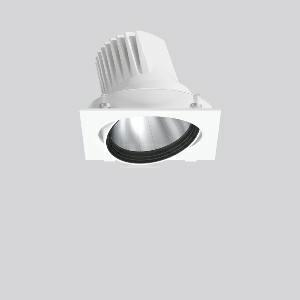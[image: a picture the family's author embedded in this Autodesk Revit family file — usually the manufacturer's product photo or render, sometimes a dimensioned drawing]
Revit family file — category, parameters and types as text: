
# Revit family: magcardo_maxi_722188_002_1_5fc1
name_source: partatom
category: Lighting Fixtures
units: mm (PartAtom-declared; Revit-internal decimal feet)

## family parameters
Cut with Voids When Loaded = No
Host = Face
Light Source = No
Part Type = Normal
Room Calculation Point = No
Round Connector Dimension = Use Diameter
Shared = No

## types (1)
- MAGCARDO maxi (1 x LED Modul 940, 3500 lm, 4000)
    Apparent Load = 25 VA
    Approval mark = CE
    CIE Flux Codes = 100 100 100 100 100
    Color Rendering = 92
    Color Temperature = 4000
    Default Elevation = 1800 mm
    Description = Series: MAGCARDO maxi
Projector unit for tool-free mounting in separate recessed frame. Luminaire top: die-cast aluminium, powder-coated. Rotation range 356° and swivel range ± 35°. Inner cover prevents view into the false ceiling. Black plastic ring and recessed LED to prevent glare from the side. Optical assembly with reflector made of MIRO-Silver with 98% total light reflection for outstanding efficiency - can be changed without tools. Best colour rendering index Ra>90. Magnetic click locking mechanism for quick and convenient installation without tools: insert the recessed frame (1, 2 or 3-lamp) with clamp fastener (no tools required), push the luminaire head with the base plate into the recessed frame and fix magnetically. Including separate LED converter with connecting cable 600 mm.High quality converter without flickering and stroboscopic effect. Through-wiring box (5 pole) available as accessory. The following accessories can be mounted without use of tools: interchangeable lenses, honeycomb louvre, clear and frosted diffusers, white interchangeable plastic ring.Modular design: recessed mounting frame must be ordered separately! 
Colour: traffic white, matt (RAL 9016)
Length: 172 mm
Width: 167 mm
Height: 137 mm
Recess height: 155 mm
Lamp: LED
Socket: without socket
Colour temperature: 4000K
Colour rendering index (CRI): 92
System power: 25 W
Rated luminous flux: 3500 lm
Luminous efficiency: 140 lm/W
Control gear: Regulated power supply
Protection class: II
Type of protection: IP 20
    Height = 0 mm  [stored 0 ft]
    Lamp = 1 x LED Modul 940
    Lamp Light Flux = 3500 lm
    Lamp count = 1
    Length = 172 mm
    Lifetime = 50000 h
    Luminous efficacy = 140 lm/W
    Manufacturer = RZB
    ModVariant = No
    Model = 722188.002.1
    Mounting Place = Ceiling, Wall
    Mounting Type = Recessed
    Number of Poles = 1
    OnlyDefault = Yes
    Power Factor = 1
    Product Name = MAGCARDO maxi
    Product group = Recessed projectors
    ProductGroupID = 401
    Protection Class = Protection class II
    Protection Degree = IP 20
    RLX_Detail_Level = 1
    RLX_Emergency_Light_Flux = 0 lm
    RLX_Emergency_Type = 0
    RLX_Emergency_Type_DB = No
    RlxData = <blob elided: 40881 chars, md5=eda8f92d>
    Socket = socket
    Standby Power = 0 W
    System Light Flux = 3500 lm
    System Power = 25 W
    Type Comments = Product without accessories
    Type Image = 722045.002.jpg
    URL = http://relux.com
    VarID = ---
    Voltage = 230 V
    Voltage Range = 220-240 V
    Weight = 0.00 kg
    Width = 167 mm

note: [stored X ft] marks values corroborated as IEEE doubles in the binary element streams (Revit-internal decimal feet)

## geometry (parser evidence)
native form markers: Blend x4, Sweep x11
no freeform markers — native parametric forms only
